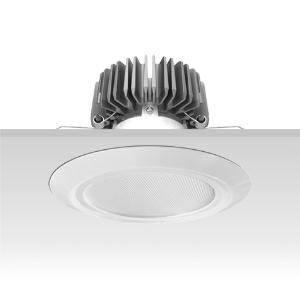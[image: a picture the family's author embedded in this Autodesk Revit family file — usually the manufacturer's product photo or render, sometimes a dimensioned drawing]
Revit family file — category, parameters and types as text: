
# Revit family: 3f_filippi_-_3f_reno_bianco_ampio_3f_filippi_-_30687_a01048_-_3f_reno_200_wh_4000-840_dali_wide___smp_wh_a2b4
name_source: partatom
category: Lighting Fixtures
units: mm (PartAtom-declared; Revit-internal decimal feet)

## family parameters
Cut with Voids When Loaded = No
Host = Face
Light Source = No
Part Type = Normal
Room Calculation Point = No
Round Connector Dimension = Use Diameter
Shared = No

## types (1)
- 3F Filippi - 3F Reno Bianco Ampio (1 x LED, 3089 lm, 36 W, 4000 K)
    Apparent Load = 36 VA
    Approval mark = CE
    CIE Flux Codes = 74 92 98 100 100
    Color Rendering = 80
    Color Temperature = 4000 K
    Control Gear = Electronic transformer
    Default Elevation = 1800 mm
    Description = ILLUMINOTECHNICAL
Luminous efficiency 100% (DLOR 100%, ULOR 0%).
Initial luminous flux of the luminaire 3089 lm.
Direct symmetric wide distribution.
Installation Interdistance Transv.D = 1.06 x hu - Long.D = 1.04 x hu.
Tabular UGR (CIE 117 - 4H-8H; S=0.25H; 70/50/20): RUG 23.5 - 23.3.
Beam angle: 70° - 69°.
Luminous efficacy 86 lm/W.
Lifetime (L90/B10): 30000 h. (tq+25°C)
Lifetime (L85/B10): 50000 h. (tq+25°C)
Lifetime (L70/B10): 80000 h. (tq+25°C)
Sudden decreased luminous flux after 50000 hours: 0% (C0).
Photobiological safety in compliance with IEC/TR 62778: RG1 low risk, (IEC 62471).
In compliance with IEC/EN 62722-2-1 - IEC/EN 62717 standards.

SOURCE
Compact LED module 4000/840.
Energy efficiency class (UE 2019/2020 - UE 2019/2015): D.
CIE 13.3 Colour rendering index: CRI >80 (R9 <50%).
IES TM-30 Fidelity Index: Rf = 84 Rg = 95.
CCT nominal colour temperature 4000 K.
Colour initial tolerance (MacAdam): SDCM 3.
Zhaga Book 3 compliant.

MECHANICAL
Passive heat dissipator in die-casting aluminium, oversized, for optimum thermal management of the LED module.
Parabolic element with graduated/concentric rings in white polycarbonate.
Transparent external lens with glossy and satin differentiated surfaces, with a cooling and anti-insect system in methacrylate (PMMA).
Fastening spring clips in stainless steel.
Dimensions: diameter 226 mm, height 146 mm. Weight 1.7 kg.
IP44 protection degree for exposed part, IP20 for recessed part.
Mechanical strength to impacts IK05 (0.7 joule).
Glow-wire test resistance 650°C.

ELECTRICAL
Wiring on a separate unit.
Halogen Free DALI-2 DATI (Parts 251, 252, 253), PUSH-DIM, electronic wiring 230V-50/60Hz, power factor 0.97 at full load, THD <25%, constant output current, SELV, class II, 1 driver, 1 DALI addresse.
Power of the luminaire 36 W.
ENEC - CE.
SAFE FLICKER: PstLM=<1 and SVM=<0.4 (IEC TR 61547-1 and IEC TR 63158), to ensure a more comfortable and safe light.
Luminaire compliant with EN 60598-2-22 for power supply from a centralised emergency system CPSS (Central Power Supply System), not incorporated in the luminaire - high risk areas excluded. The default power and flux are 100% in AC and 100% in DC.
Ambient temperature from 0°C to +25°C.
Temperature class T6 max 85°C.
Relative humidity UR: <85%.

INSTALLATION
Pull-up recessed fitting.
False ceiling carving: 200 mm.
All accessories dedicated to this product are available on the Catalog and on our website www.3F-Filippi.com.

ACCESSORIES
A01048 - Anti-glare microprismatic SMP diffuser in methacrylate (PMMA), locked and in line with the trim, in white polycarbonate.

APPLICATIONS
Suitable product for food production plants (HACCP), IFS (Food Version 6), BRC (GSFS Food Version 7).
Environments: architectural, commercial, exhibition areas, transit areas, corridors, shops, display windows, service areas.
In false ceilings with narrow voids.

LIGHT MANAGEMENT
Recommended minimum setting: 10%.
The luminaire, equipped with (DALI-2 DATI) driver, can be controlled manually with 3F Easy Dim technology or automatically/manually with wired or wireless DALI/D2D control systems.
The D2D driver guarantees interoperability with other devices with the same certification by making the following information available:
Device Data (Part 251), Energy Report (Part 252), Diagnosis & Maintenance (Part 253).
In electrical systems without a regulation system (manual or automatic) and DALI bus, a suitable jumper must be made on the DA-DA terminals of the appliance.

WARNING
Luminaire designed for disposal/recycling at end-of-life.
Replaceable (LED only) light source by a professional. Replaceable control gear by a professional.
    Height = 0 mm  [stored 0 ft]
    Lamp = 1 x LED
    Lamp Light Flux = 3089 lm
    Lamp Power = 36 W
    Lamp count = 1
    Length = 226 mm
    Lifetime = 50000 h
    Luminous efficacy = 86 lm/W
    Manufacturer = 3F Filippi
    ModVariant = No
    Model = 3F Filippi - 30687+A01048 - 3F Reno 200 WH 4000-840 DALI WIDE + SMP WH
    Mounting Place = Ceiling
    Mounting Type = Recessed
    Number of Poles = 1
    OnlyDefault = Yes
    Power Factor = 1
    Product Name = 3F Filippi - 3F Reno Bianco Ampio
    Product group = recessed luminaire
    ProductGroupID = 4
    Protection Class = Protection class II
    Protection Degree = IP 20
    RLX_Detail_Level = 1
    RLX_Emergency_Light_Flux = 0 lm
    RLX_Emergency_Type = 0
    RLX_Emergency_Type_DB = No
    RlxData = <blob elided: 96793 chars, md5=004501b9>
    Socket = socket
    Standby Power = 0 W
    System Light Flux = 3089 lm
    System Power = 36 W
    Type Comments = Product without accessories
    Type Image = 3ffilippi_3f_reno_200_wh_vs_smp.jpg
    URL = http://relux.com
    VarID = ---
    Voltage = 0 V
    Weight = 0.00 kg
    Width = 0 mm  [stored 0 ft]

note: [stored X ft] marks values corroborated as IEEE doubles in the binary element streams (Revit-internal decimal feet)

## geometry (parser evidence)
native form markers: Blend x4, Sweep x10
no freeform markers — native parametric forms only
